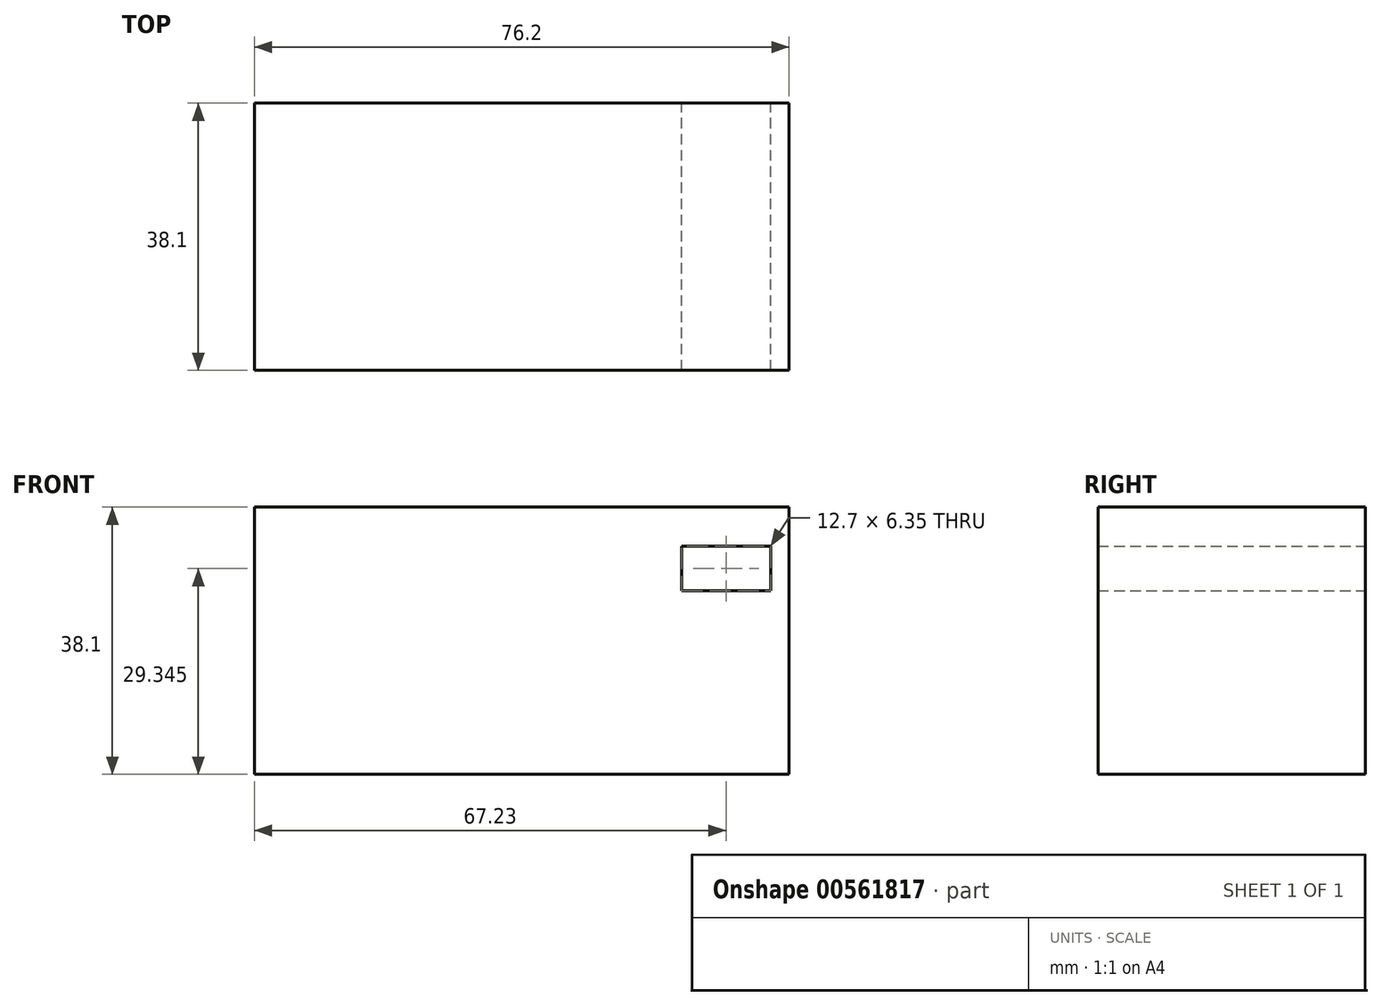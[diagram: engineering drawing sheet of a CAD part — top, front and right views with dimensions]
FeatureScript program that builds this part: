
annotation { "Feature Type Name" : "Feature", "Feature Type Description" : "" }
export const myFeature = defineFeature(function(context is Context, id is Id, definition is map)
    precondition{}
    {
        {
            var Q0;
            Q0=qCreatedBy(makeId("Front.planeOp"),FACE);
            var sketch = newSketch(context, id + "F0", { "sketchPlane" : qUnion([Q0])});
            skLineSegment(sketch, "E0.bottom", {"start": v(-38.1, 19.05) * mm, "end": v(38.1, 19.05) * mm});
            skLineSegment(sketch, "E0.top", {"start": v(-38.1, -19.05) * mm, "end": v(38.1, -19.05) * mm});
            skLineSegment(sketch, "E0.left", {"start": v(-38.1, 19.05) * mm, "end": v(-38.1, -19.05) * mm});
            skLineSegment(sketch, "E0.right", {"start": v(38.1, 19.05) * mm, "end": v(38.1, -19.05) * mm});
            skPoint(sketch, "E0.middle", {"position": v(0, 0) * mm});
            skSolve(sketch);
        }
        {
            var Q0;
            Q0 = qSketchRegion(id + "F0", true);
            extrude(context, id + "F1", {"entities" : qUnion([Q0]), "depth" : 38.1 * mm, "offsetDistance" : 25.4 * mm});
        }
        {
            var Q0;
            Q0=qCreatedBy(makeId("Front.planeOp"),FACE);
            var sketch = newSketch(context, id + "F2", { "sketchPlane" : qUnion([Q0])});
            skLineSegment(sketch, "E1.bottom", {"start": v(22.78, 7.12) * mm, "end": v(35.48, 7.12) * mm});
            skLineSegment(sketch, "E1.top", {"start": v(22.78, 13.47) * mm, "end": v(35.48, 13.47) * mm});
            skLineSegment(sketch, "E1.left", {"start": v(22.78, 7.12) * mm, "end": v(22.78, 13.47) * mm});
            skLineSegment(sketch, "E1.right", {"start": v(35.48, 7.12) * mm, "end": v(35.48, 13.47) * mm});
            skPoint(sketch, "E1.middle", {"position": v(29.13, 10.3) * mm});
            skSolve(sketch);
        }
        {
            var Q0;
            Q0 = qSketchRegion(id + "F2", true);
            extrude(context, id + "F3", {"entities" : qUnion([Q0]), "operationType" : NewBodyOperationType.REMOVE, "depth" : 50.55 * mm, "offsetDistance" : 25.4 * mm});
        }
    });
